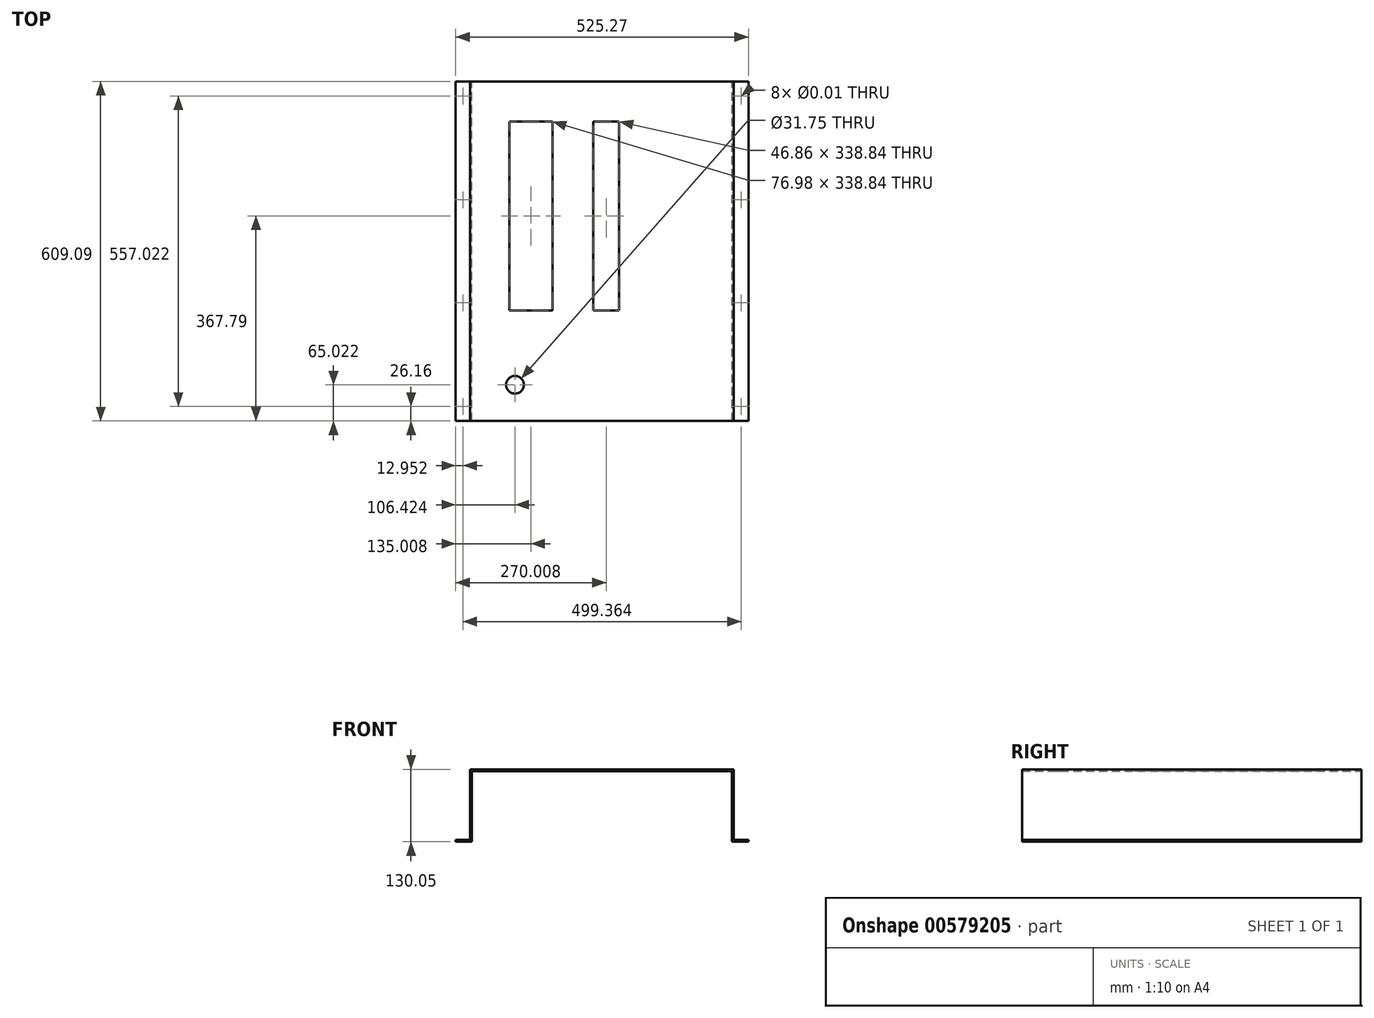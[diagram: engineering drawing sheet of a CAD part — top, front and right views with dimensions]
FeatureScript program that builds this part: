
annotation { "Feature Type Name" : "Feature", "Feature Type Description" : "" }
export const myFeature = defineFeature(function(context is Context, id is Id, definition is map)
    precondition{}
    {
        {
            var Q0;
            Q0=qCreatedBy(makeId("Front.planeOp"),FACE);
            var sketch = newSketch(context, id + "F0", { "sketchPlane" : qUnion([Q0])});
            skLineSegment(sketch, "E0", {"start": v(0, 0) * mm, "end": v(-26.16, 0) * mm});
            skLineSegment(sketch, "E1", {"start": v(-26.16, 0) * mm, "end": v(-26.16, 126.87) * mm});
            skLineSegment(sketch, "E2", {"start": v(-26.16, 126.87) * mm, "end": v(-499.36, 126.87) * mm});
            skLineSegment(sketch, "E3", {"start": v(-499.36, 126.87) * mm, "end": v(-499.36, 0) * mm});
            skLineSegment(sketch, "E4", {"start": v(-499.36, 0) * mm, "end": v(-525.27, 0) * mm});
            skLineSegment(sketch, "E5", {"start": v(-525.27, 0) * mm, "end": v(-525.27, -3.18) * mm});
            skLineSegment(sketch, "E6", {"start": v(-525.27, -3.18) * mm, "end": v(-496.19, -3.18) * mm});
            skLineSegment(sketch, "E7", {"start": v(-496.19, -3.18) * mm, "end": v(-496.19, 123.7) * mm});
            skLineSegment(sketch, "E8", {"start": v(-496.19, 123.7) * mm, "end": v(-29.34, 123.7) * mm});
            skLineSegment(sketch, "E9", {"start": v(-29.34, 123.7) * mm, "end": v(-29.34, -3.18) * mm});
            skLineSegment(sketch, "E10", {"start": v(-29.34, -3.18) * mm, "end": v(0, -3.18) * mm});
            skLineSegment(sketch, "E11", {"start": v(0, -3.18) * mm, "end": v(0, 0) * mm});
            skSolve(sketch);
        }
        {
            var Q0;
            Q0 = qSketchRegion(id + "F0", true);
            extrude(context, id + "F1", {"entities" : qUnion([Q0]), "depth" : 609.1 * mm, "offsetDistance" : 25.4 * mm});
        }
        {
            var Q0;
            Q0=makeQuery(id+"F1.opExtrude","SWEPT_FACE",FACE,{"disambiguationData":[OSD([sQuery(id+"F0.wireOp",EDGE,"E4")])]});
            var sketch = newSketch(context, id + "F2", { "sketchPlane" : qUnion([Q0])});
            skPoint(sketch, "E12", {"position": v(-512.32, -25.9) * mm});
            skPoint(sketch, "E13", {"position": v(-512.32, -212.1) * mm});
            skPoint(sketch, "E14", {"position": v(-512.32, -397) * mm});
            skPoint(sketch, "E15", {"position": v(-512.32, -582.93) * mm});
            skPoint(sketch, "E16", {"position": v(-12.95, -582.93) * mm});
            skPoint(sketch, "E17", {"position": v(-12.95, -397) * mm});
            skPoint(sketch, "E18", {"position": v(-12.95, -212.09) * mm});
            skPoint(sketch, "E19", {"position": v(-12.95, -25.9) * mm});
            skSolve(sketch);
        }
        {
            var Q0;
            Q0=makeQuery(id+"F1.opExtrude","SWEPT_FACE",FACE,{"disambiguationData":[OSD([sQuery(id+"F0.wireOp",EDGE,"E2")])]});
            var sketch = newSketch(context, id + "F3", { "sketchPlane" : qUnion([Q0])});
            skLineSegment(sketch, "E20.bottom", {"start": v(-428.75, -71.88) * mm, "end": v(-351.77, -71.88) * mm});
            skLineSegment(sketch, "E20.top", {"start": v(-428.75, -410.72) * mm, "end": v(-351.77, -410.72) * mm});
            skLineSegment(sketch, "E20.left", {"start": v(-428.75, -71.88) * mm, "end": v(-428.75, -410.72) * mm});
            skLineSegment(sketch, "E20.right", {"start": v(-351.77, -71.88) * mm, "end": v(-351.77, -410.72) * mm});
            skLineSegment(sketch, "E21.bottom", {"start": v(-278.7, -71.88) * mm, "end": v(-231.83, -71.88) * mm});
            skLineSegment(sketch, "E21.top", {"start": v(-278.7, -410.72) * mm, "end": v(-231.83, -410.72) * mm});
            skLineSegment(sketch, "E21.left", {"start": v(-278.7, -71.88) * mm, "end": v(-278.7, -410.72) * mm});
            skLineSegment(sketch, "E21.right", {"start": v(-231.83, -71.88) * mm, "end": v(-231.83, -410.72) * mm});
            skPoint(sketch, "E22", {"position": v(-390.26, -71.88) * mm});
            skPoint(sketch, "E23", {"position": v(-255.26, -71.88) * mm});
            skSolve(sketch);
        }
        {
            var Q0;
            Q0 = qSketchRegion(id + "F3", true);
            extrude(context, id + "F4", {"entities" : qUnion([Q0]), "operationType" : NewBodyOperationType.REMOVE, "oppositeDirection" : true, "depth" : 25.4 * mm, "offsetDistance" : 25.4 * mm});
        }
        {
            var Q0;
            Q0=makeQuery(id+"F1.opExtrude","SWEPT_FACE",FACE,{"disambiguationData":[OSD([sQuery(id+"F0.wireOp",EDGE,"E2")])]});
            var sketch = newSketch(context, id + "F5", { "sketchPlane" : qUnion([Q0])});
            skLineSegment(sketch, "E24.bottom", {"start": v(-435.26, -71.88) * mm, "end": v(-345.26, -71.88) * mm});
            skLineSegment(sketch, "E24.top", {"start": v(-435.26, -471.88) * mm, "end": v(-345.26, -471.88) * mm});
            skLineSegment(sketch, "E24.left", {"start": v(-435.26, -71.88) * mm, "end": v(-435.26, -471.88) * mm});
            skLineSegment(sketch, "E24.right", {"start": v(-345.26, -71.88) * mm, "end": v(-345.26, -471.88) * mm});
            skLineSegment(sketch, "E25.bottom", {"start": v(-345.26, -71.88) * mm, "end": v(-285.26, -71.88) * mm});
            skLineSegment(sketch, "E25.top", {"start": v(-345.26, -471.88) * mm, "end": v(-285.26, -471.88) * mm});
            skLineSegment(sketch, "E25.right", {"start": v(-285.26, -71.88) * mm, "end": v(-285.26, -471.88) * mm});
            skLineSegment(sketch, "E26.bottom", {"start": v(-285.26, -71.88) * mm, "end": v(-225.26, -71.88) * mm});
            skLineSegment(sketch, "E26.top", {"start": v(-285.26, -471.88) * mm, "end": v(-225.26, -471.88) * mm});
            skLineSegment(sketch, "E26.right", {"start": v(-225.26, -71.88) * mm, "end": v(-225.26, -471.88) * mm});
            skLineSegment(sketch, "E27.bottom", {"start": v(-225.26, -71.88) * mm, "end": v(-165.26, -71.88) * mm});
            skLineSegment(sketch, "E27.top", {"start": v(-225.26, -471.88) * mm, "end": v(-165.26, -471.88) * mm});
            skLineSegment(sketch, "E27.right", {"start": v(-165.26, -71.88) * mm, "end": v(-165.26, -471.88) * mm});
            skSolve(sketch);
        }
        {
            var Q0;
            Q0=makeQuery(id+"F5.imprint","IMPRINT",FACE,{"disambiguationData":[TD([[makeQuery(id+"F5.imprint","IMPRINT",EDGE,{"derivedFrom":sQuery(id+"F5.wireOp",EDGE,"E24.top")}),-1.0]])]});
            var sketch = newSketch(context, id + "F6", { "sketchPlane" : qUnion([Q0])});
            skCircle(sketch, "E28", {"center": v(-418.85, -544.07) * mm, "radius": 15.88 * mm});
            skSolve(sketch);
        }
        {
            var Q0;
            Q0=makeQuery(id+"F6.imprint","IMPRINT",FACE,{"disambiguationData":[TD([[makeQuery(id+"F6.imprint","IMPRINT",EDGE,{"derivedFrom":sQuery(id+"F6.wireOp",EDGE,"E28")}),1.0]])]});
            extrude(context, id + "F7", {"entities" : qUnion([Q0]), "operationType" : NewBodyOperationType.REMOVE, "oppositeDirection" : true, "depth" : 25.4 * mm, "offsetDistance" : 25.4 * mm});
        }
        {
            var Q0;
            Q0=sQuery(id+"F2.wireOp",VERTEX,"E12");
            var Q1;
            Q1=sQuery(id+"F2.wireOp",VERTEX,"E13");
            var Q2;
            Q2=sQuery(id+"F2.wireOp",VERTEX,"E14");
            var Q3;
            Q3=sQuery(id+"F2.wireOp",VERTEX,"E15");
            var Q4;
            Q4=sQuery(id+"F2.wireOp",VERTEX,"E16");
            var Q5;
            Q5=sQuery(id+"F2.wireOp",VERTEX,"E17");
            var Q6;
            Q6=sQuery(id+"F2.wireOp",VERTEX,"E18");
            var Q7;
            Q7=sQuery(id+"F2.wireOp",VERTEX,"E19");
            var Q8;
            Q8=makeQuery(id+"F1.opExtrude","SWEPT_BODY",BODY,{"disambiguationData":[OSD([sQuery(id+"F0.wireOp",EDGE,"E0"),sQuery(id+"F0.wireOp",EDGE,"E1"),sQuery(id+"F0.wireOp",EDGE,"E2"),sQuery(id+"F0.wireOp",EDGE,"E3"),sQuery(id+"F0.wireOp",EDGE,"E4"),sQuery(id+"F0.wireOp",EDGE,"E5"),sQuery(id+"F0.wireOp",EDGE,"E6"),sQuery(id+"F0.wireOp",EDGE,"E7"),sQuery(id+"F0.wireOp",EDGE,"E8"),sQuery(id+"F0.wireOp",EDGE,"E9"),sQuery(id+"F0.wireOp",EDGE,"E10"),sQuery(id+"F0.wireOp",EDGE,"E11")])]});
            hole(context, id + "F8", {"style" : HoleStyle.SIMPLE, "endStyle" : HoleEndStyle.THROUGH, "standardTappedOrClearance" : lookupTablePath({ "standard" : "ANSI", "size" : "9/32 (0.28)", "type" : "Drilled" }), "standardBlindInLast" : lookupTablePath({ "standard" : "ANSI", "size" : "9/32", "type" : "Drilled" }), "holeDiameter" : 9 / 812.8 * mm, "isTappedThrough" : true, "tappedDepth" : 8.9 * mm, "tapClearance" : 1, "locations" : qUnion([Q0, Q1, Q2, Q3, Q4, Q5, Q6, Q7]), "scope" : qUnion([Q8])});
        }
    });
